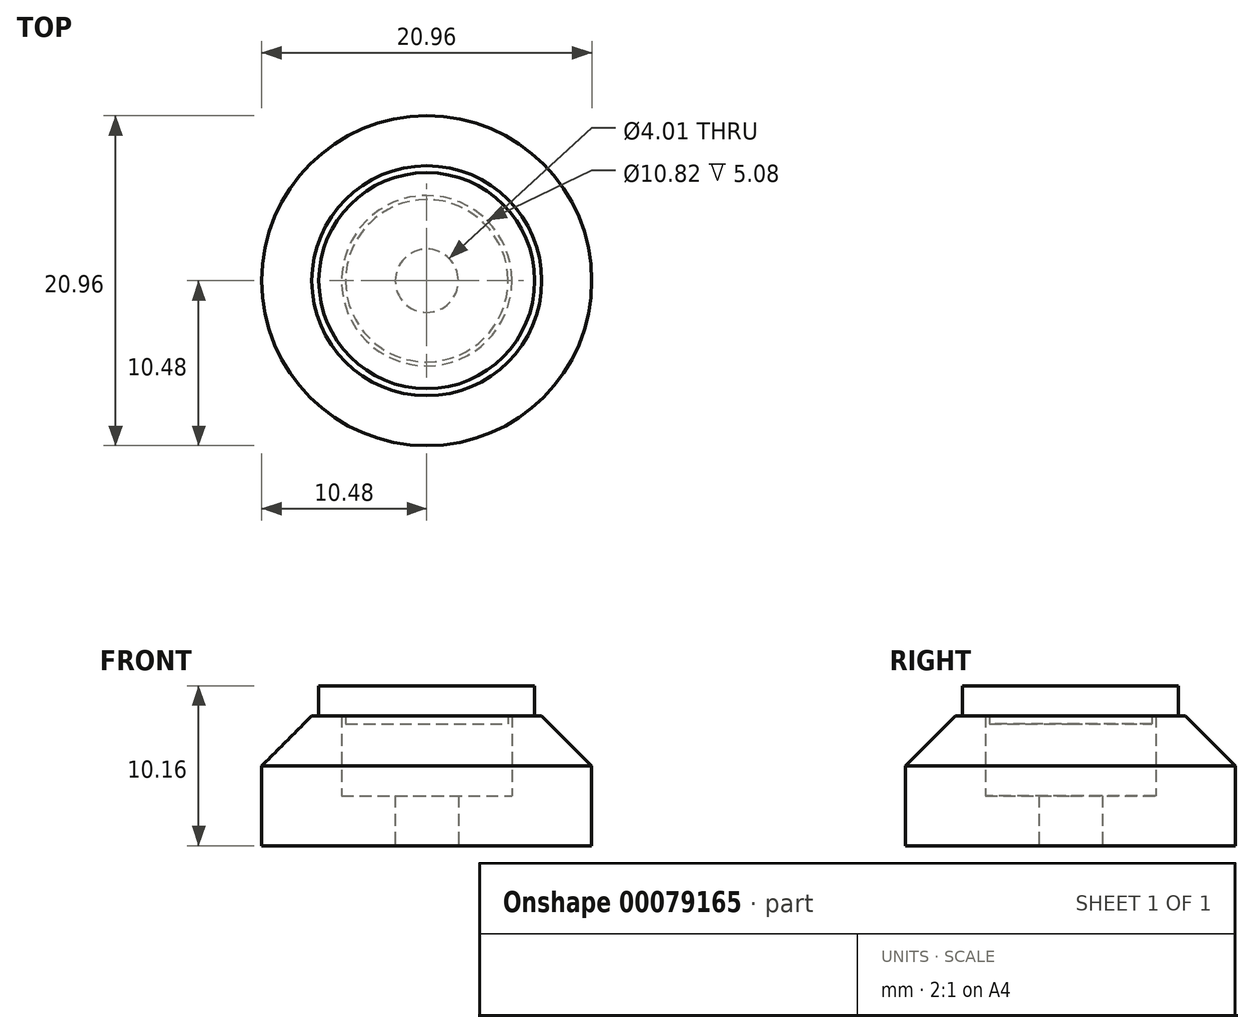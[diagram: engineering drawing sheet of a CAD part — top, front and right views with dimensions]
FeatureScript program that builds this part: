
annotation { "Feature Type Name" : "Feature", "Feature Type Description" : "" }
export const myFeature = defineFeature(function(context is Context, id is Id, definition is map)
    precondition{}
    {
        {
            var Q0;
            Q0=qCreatedBy(makeId("Front.planeOp"),FACE);
            var sketch = newSketch(context, id + "F0", { "sketchPlane" : qUnion([Q0])});
            skLineSegment(sketch, "E0", {"start": v(2, 0) * mm, "end": v(2, 3.18) * mm});
            skLineSegment(sketch, "E1", {"start": v(2, 3.18) * mm, "end": v(5.41, 3.18) * mm});
            skLineSegment(sketch, "E2", {"start": v(5.41, 3.18) * mm, "end": v(5.41, 8.26) * mm});
            skLineSegment(sketch, "E3", {"start": v(5.41, 8.26) * mm, "end": v(10.48, 8.26) * mm});
            skLineSegment(sketch, "E4", {"start": v(10.48, 8.26) * mm, "end": v(10.48, 0) * mm});
            skLineSegment(sketch, "E5", {"start": v(10.48, 0) * mm, "end": v(2, 0) * mm});
            skLineSegment(sketch, "E6", {"start": v(0, 0) * mm, "end": v(0, 8.26) * mm, "construction": true});
            skSolve(sketch);
        }
        {
            var Q0;
            Q0 = qSketchRegion(id + "F0", true);
            var Q1;
            Q1=sQuery(id+"F0.wireOp",EDGE,"E6");
            revolve(context, id + "F1", {"entities" : qUnion([Q0]), "axis" : qUnion([Q1]), "revolveType" : RevolveType.FULL});
        }
        {
            var Q0;
            Q0=makeQuery(id+"F1.opRevolve","SWEPT_EDGE",EDGE,{"disambiguationData":[OSD([sQuery(id+"F0.wireOp",EDGE,"E3"),sQuery(id+"F0.wireOp",EDGE,"E4")])]});
            chamfer(context, id + "F2", {"entities" : qUnion([Q0]), "width" : 3.17 * mm, "tangentPropagation" : true});
        }
        {
            var Q0;
            Q0=qCreatedBy(makeId("Front.planeOp"),FACE);
            var sketch = newSketch(context, id + "F3", { "sketchPlane" : qUnion([Q0])});
            skLineSegment(sketch, "E7", {"start": v(0, 7.75) * mm, "end": v(0, 10.16) * mm});
            skLineSegment(sketch, "E8", {"start": v(0, 10.16) * mm, "end": v(6.86, 10.16) * mm});
            skLineSegment(sketch, "E9", {"start": v(6.86, 10.16) * mm, "end": v(6.86, 8.26) * mm});
            skLineSegment(sketch, "E10", {"start": v(6.86, 8.26) * mm, "end": v(5.16, 8.26) * mm});
            skLineSegment(sketch, "E11", {"start": v(5.16, 8.26) * mm, "end": v(5.16, 7.75) * mm});
            skLineSegment(sketch, "E12", {"start": v(5.16, 7.75) * mm, "end": v(0, 7.75) * mm});
            skSolve(sketch);
        }
        {
            var Q0;
            Q0 = qSketchRegion(id + "F3", true);
            var Q1;
            Q1=sQuery(id+"F3.wireOp",EDGE,"E7");
            revolve(context, id + "F4", {"entities" : qUnion([Q0]), "axis" : qUnion([Q1]), "revolveType" : RevolveType.FULL});
        }
    });
